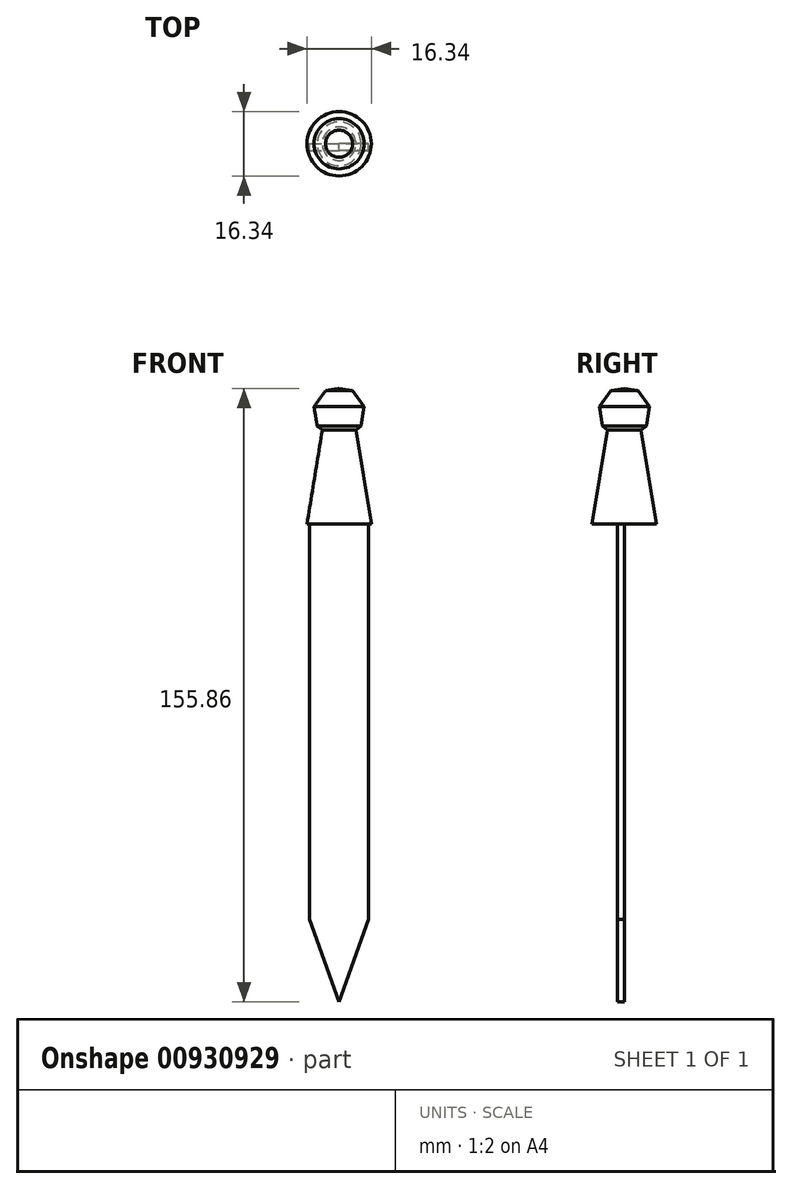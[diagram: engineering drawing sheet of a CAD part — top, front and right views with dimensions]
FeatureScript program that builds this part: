
annotation { "Feature Type Name" : "Feature", "Feature Type Description" : "" }
export const myFeature = defineFeature(function(context is Context, id is Id, definition is map)
    precondition{}
    {
        {
            var Q0;
            Q0=qCreatedBy(makeId("Front.planeOp"),FACE);
            var sketch = newSketch(context, id + "F0", { "sketchPlane" : qUnion([Q0])});
            skLineSegment(sketch, "E0.right", {"start": v(-7.5, 45.37) * mm, "end": v(-7.5, -55.16) * mm});
            skLineSegment(sketch, "E1", {"start": v(-7.5, -55.16) * mm, "end": v(0, -76.1) * mm});
            skLineSegment(sketch, "E2", {"start": v(0, 45.37) * mm, "end": v(-7.5, 45.37) * mm});
            skLineSegment(sketch, "E3", {"start": v(-2.94, 71.52) * mm, "end": v(-2.94, 71.54) * mm});
            skArc(sketch, "E4.cCircle", {"start": v(0, 82.02) * mm, "mid": v(-0.15, 82.02) * mm, "end": v(-0.3, 82.01) * mm, "construction": true});
            skLineSegment(sketch, "E4.2", {"start": v(0.3, 70.7) * mm, "end": v(0, 70.8) * mm});
            skLineSegment(sketch, "E4.6", {"start": v(-0.3, 82.01) * mm, "end": v(0, 81.9) * mm});
            skLineSegment(sketch, "E5", {"start": v(0, -89.17) * mm, "end": v(0, 70.8) * mm, "construction": true});
            skArc(sketch, "E6.trimOffspring", {"start": v(0, 70.7) * mm, "mid": v(0.15, 70.7) * mm, "end": v(0.3, 70.7) * mm, "construction": true});
            skLineSegment(sketch, "E7.trimOffspring", {"start": v(0, 81.9) * mm, "end": v(0, 82.02) * mm, "construction": true});
            skLineSegment(sketch, "E8.MirrorCS", {"start": v(7.5, 45.37) * mm, "end": v(7.5, -55.16) * mm});
            skLineSegment(sketch, "E9.MirrorCS", {"start": v(7.5, -55.16) * mm, "end": v(0, -76.1) * mm});
            skLineSegment(sketch, "E10.MirrorCS", {"start": v(0, 45.37) * mm, "end": v(7.5, 45.37) * mm});
            skPoint(sketch, "E11.MirrorCS.end.orphan", {"position": v(-7.5, 45.37) * mm});
            skPoint(sketch, "E11.MirrorCS.start.orphan", {"position": v(-15, 45.37) * mm});
            skSolve(sketch);
        }
        {
            var Q0;
            Q0 = qSketchRegion(id + "F0", true);
            extrude(context, id + "F1", {"entities" : qUnion([Q0]), "depth" : 1.78 * mm, "offsetDistance" : 25.4 * mm});
        }
        {
            var Q0;
            Q0=qCreatedBy(makeId("Front.planeOp"),FACE);
            var sketch = newSketch(context, id + "F2", { "sketchPlane" : qUnion([Q0])});
            skLineSegment(sketch, "E12", {"start": v(0, 45.35) * mm, "end": v(-8.17, 45.35) * mm});
            skLineSegment(sketch, "E13", {"start": v(-8.17, 45.35) * mm, "end": v(-4.26, 69.25) * mm});
            skCircle(sketch, "E14.cCircle", {"center": v(0, 73.63) * mm, "radius": 6.54 * mm, "construction": true});
            skLineSegment(sketch, "E14.1", {"start": v(-4.26, 69.25) * mm, "end": v(-5.56, 70.19) * mm});
            skLineSegment(sketch, "E14.2", {"start": v(-5.56, 70.19) * mm, "end": v(-6.37, 75.13) * mm});
            skLineSegment(sketch, "E14.3", {"start": v(-6.37, 75.13) * mm, "end": v(-3.44, 79.2) * mm});
            skLineSegment(sketch, "E14.4", {"start": v(-3.44, 79.2) * mm, "end": v(0, 79.76) * mm});
            skPoint(sketch, "E15.orphan", {"position": v(3.44, 68.07) * mm});
            skPoint(sketch, "E16.orphan", {"position": v(-1.5, 67.26) * mm});
            skPoint(sketch, "E17.orphan", {"position": v(0, 83.2) * mm});
            skLineSegment(sketch, "E18", {"start": v(0, 45.35) * mm, "end": v(0, 79.76) * mm});
            skSolve(sketch);
        }
        {
            var Q0;
            Q0=qCreatedBy(makeId("Front.planeOp"),FACE);
            var sketch = newSketch(context, id + "F3", { "sketchPlane" : qUnion([Q0])});
            skLineSegment(sketch, "E19", {"start": v(0, 41.44) * mm, "end": v(0, 81.76) * mm, "construction": true});
            skSolve(sketch);
        }
        {
            var Q0;
            Q0 = qSketchRegion(id + "F2", true);
            var Q1;
            Q1=sQuery(id+"F3.wireOp",EDGE,"E19");
            revolve(context, id + "F4", {"operationType" : NewBodyOperationType.ADD, "surfaceOperationType" : NewSurfaceOperationType.NEW, "entities" : qUnion([Q0]), "axis" : qUnion([Q1]), "revolveType" : RevolveType.FULL});
        }
    });
